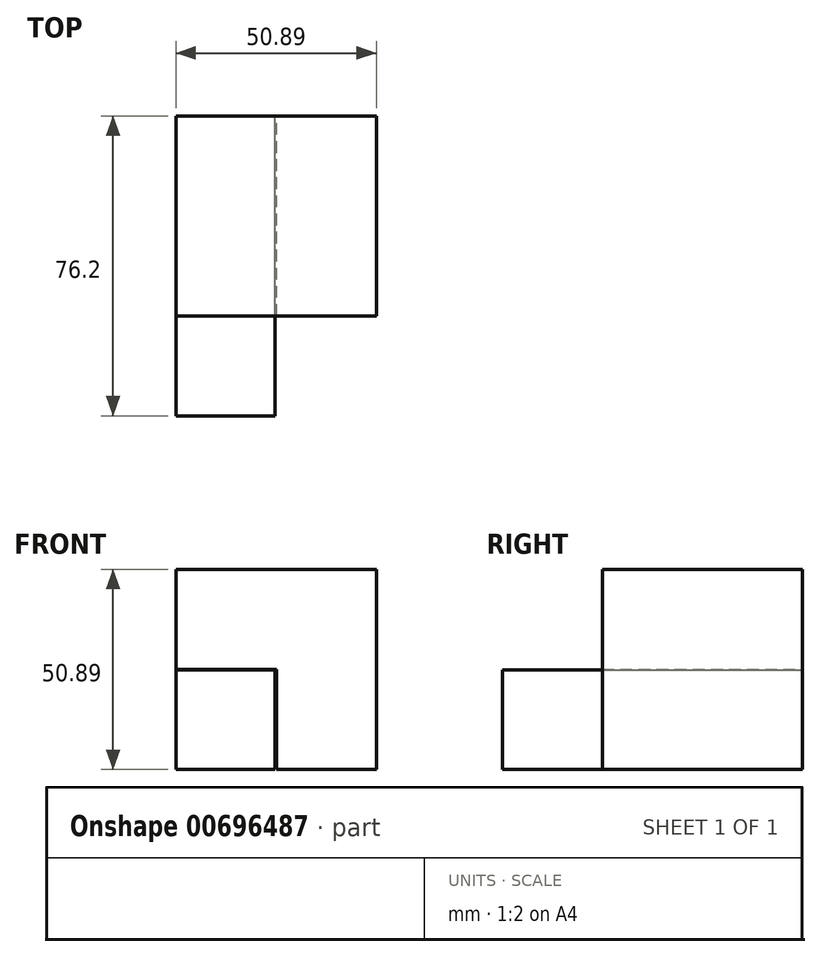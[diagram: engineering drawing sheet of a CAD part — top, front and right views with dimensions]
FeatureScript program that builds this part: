
annotation { "Feature Type Name" : "Feature", "Feature Type Description" : "" }
export const myFeature = defineFeature(function(context is Context, id is Id, definition is map)
    precondition{}
    {
        {
            var Q0;
            Q0=qCreatedBy(makeId("Front.planeOp"),FACE);
            var sketch = newSketch(context, id + "F0", { "sketchPlane" : qUnion([Q0])});
            skPoint(sketch, "E0.start.orphan", {"position": v(1.62, 0) * mm});
            skLineSegment(sketch, "E1", {"start": v(0, 0) * mm, "end": v(0, 25.5) * mm});
            skLineSegment(sketch, "E2", {"start": v(0, 25.5) * mm, "end": v(25.5, 25.5) * mm});
            skLineSegment(sketch, "E3", {"start": v(25.5, 25.5) * mm, "end": v(25.5, 0) * mm});
            skLineSegment(sketch, "E4", {"start": v(0, 0) * mm, "end": v(25.5, 0) * mm});
            skLineSegment(sketch, "E5", {"start": v(0, 0) * mm, "end": v(0, 50.89) * mm});
            skLineSegment(sketch, "E6", {"start": v(0, 50.89) * mm, "end": v(50.89, 50.89) * mm});
            skLineSegment(sketch, "E7", {"start": v(50.89, 50.89) * mm, "end": v(50.89, 0) * mm});
            skLineSegment(sketch, "E8", {"start": v(50.89, 0) * mm, "end": v(0, 0) * mm});
            skSolve(sketch);
        }
        {
            var Q0;
            {var subQ2=sQuery(id+"F0.wireOp",EDGE,"E2");Q0=makeQuery(id+"F0.imprint","IMPRINT",FACE,{"disambiguationData":[TD([[makeQuery(id+"F0.imprint","IMPRINT",EDGE,{"derivedFrom":subQ2}),1.0]])]});}
            extrude(context, id + "F1", {"entities" : qUnion([Q0]), "depth" : 50.8 * mm, "offsetDistance" : 25.4 * mm});
        }
        {
            var Q0;
            Q0=qCreatedBy(makeId("Front.planeOp"),FACE);
            var sketch = newSketch(context, id + "F2", { "sketchPlane" : qUnion([Q0])});
            skLineSegment(sketch, "E9", {"start": v(0, 0) * mm, "end": v(0, 25.3) * mm});
            skLineSegment(sketch, "E10", {"start": v(0, 0) * mm, "end": v(25.11, 0) * mm});
            skLineSegment(sketch, "E11", {"start": v(25.11, 0) * mm, "end": v(25.11, 25.3) * mm});
            skLineSegment(sketch, "E12", {"start": v(25.11, 25.3) * mm, "end": v(0, 25.3) * mm});
            skSolve(sketch);
        }
        {
            var Q0;
            Q0 = qSketchRegion(id + "F2", true);
            extrude(context, id + "F3", {"entities" : qUnion([Q0]), "depth" : 76.2 * mm, "offsetDistance" : 25.4 * mm});
        }
    });
